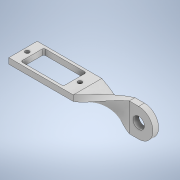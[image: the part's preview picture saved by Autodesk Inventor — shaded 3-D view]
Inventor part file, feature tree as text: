
AUTODESK INVENTOR PART (.ipt)
format: ipt  version: 2020.3 (Build 243373000, 373)  size: 182,272 bytes
history: native  units: mm
features: sketch x3, extrude x2, helix x1, plane x1, projected_geometry x1
ambient origin geometry x8: Origin, YZ Plane, XZ Plane, XY Plane, X Axis, Y Axis, Z Axis, Center Point
bodies: Body1 (feature_tree)
feature tree (8):
  extrude  "Extrusion2"  Depth=3.0mm TaperAngle=0.0deg
  helix  "Coil2"  [1 undecoded]
  plane  "Work Plane2"
  extrude  "Extrusion3"  [1 undecoded]
  sketch  "Sketch1"  dims[d30=5.0mm d31=3.0mm d32=0.0mm]
  sketch  "Sketch5"  dims[d33=100.0mm d34=10.0mm d35=2.5mm d36=0.0mm d37=90.0deg d38=90.0deg d39=0.0mm d40=0.0mm d43=3.0mm d44=0.0mm]
  projected_geometry  "Projected Loop2"
  sketch  "Sketch6"
note: 2 required parameter values undecoded (feature->parameter linkage not recoverable at this tier; creation-order binding heuristic only, values carry confidence <= 0.55)
